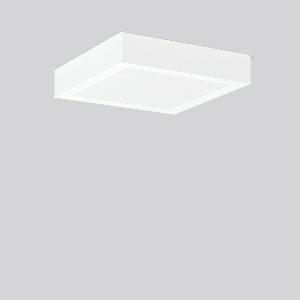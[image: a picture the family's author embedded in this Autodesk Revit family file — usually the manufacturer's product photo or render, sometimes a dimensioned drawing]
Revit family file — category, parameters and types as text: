
# Revit family: toledo_flat_square_a_672269_002_1_89_02b8
name_source: partatom
category: Lighting Fixtures
units: mm (PartAtom-declared; Revit-internal decimal feet)

## family parameters
Cut with Voids When Loaded = No
Host = Face
Light Source = No
Part Type = Normal
Room Calculation Point = No
Round Connector Dimension = Use Diameter
Shared = No

## types (1)
- TOLEDO FLAT square A (1 x LED Modul 840, 2200 lm, 4000)
    Apparent Load = 23 VA
    CIE Flux Codes = 49 80 96 100 100
    Color Rendering = 80
    Color Temperature = 4000
    Default Elevation = 1800 mm
    Description = Series: TOLEDO FLAT square
Ultra thin surface mounted downlight. For escape route illumination. Surface mounted housing: sheet steel, powder-coated. Square cover plate: die-cast aluminium, powder coated. Light guide and diffuser made of non-yellowing PMMA, opal matt. Driver integrated. Suitable for connection to central battery systems. With AC Control monitoring module for LUXIFAIR central battery units. 
Colour: white
Length: 300 mm
Width: 300 mm
Height: 58 mm
Weight: 3.64 kg
Operating mode: maintained power mode
Lamp: LED
Socket: without socket
Colour temperature: 4000K
Colour rendering index (CRI): 80
System power: 23 W
Rated luminous flux: 2200 lm
Luminous flux, emergency: 2200 lm
System power, emergency: 23 W
Control gear: Regulated power supply
Protection class: I
Type of protection: IP 40
    Height = 58 mm
    Lamp = 1 x LED Modul 840
    Lamp Light Flux = 2200 lm
    Lamp count = 1
    Length = 300 mm
    Lifetime = 50000 h
    Luminous efficacy = 96 lm/W
    Manufacturer = RZB
    ModVariant = No
    Model = 672269.002.1.89
    Mounting Place = Ceiling
    Mounting Type = Surface mounted
    Number of Poles = 1
    OnlyDefault = Yes
    Power Factor = 1
    Product Name = TOLEDO FLAT square A
    Product group = Surface mounted downlights
    ProductGroupID = 302
    Protection Class = Protection class I
    Protection Degree = IP 40
    RLX_Detail_Level = 1
    RLX_Emergency_Light_Flux = 2200 lm
    RLX_Emergency_Type = 3
    RLX_Emergency_Type_DB = Yes
    RlxData = <blob elided: 13697 chars, md5=7d9b12d4>
    Socket = socket
    Standby Power = 0 W
    System Light Flux = 2200 lm
    System Power = 23 W
    Type Comments = Product without accessories
    Type Image = 901554.002.jpg
    URL = http://relux.com
    VarID = ---
    Voltage = 230 V
    Voltage Range = 220-240 V
    Weight = 0.00 kg
    Width = 300 mm

## geometry (parser evidence)
native form markers: Sweep x11
no freeform markers — native parametric forms only
